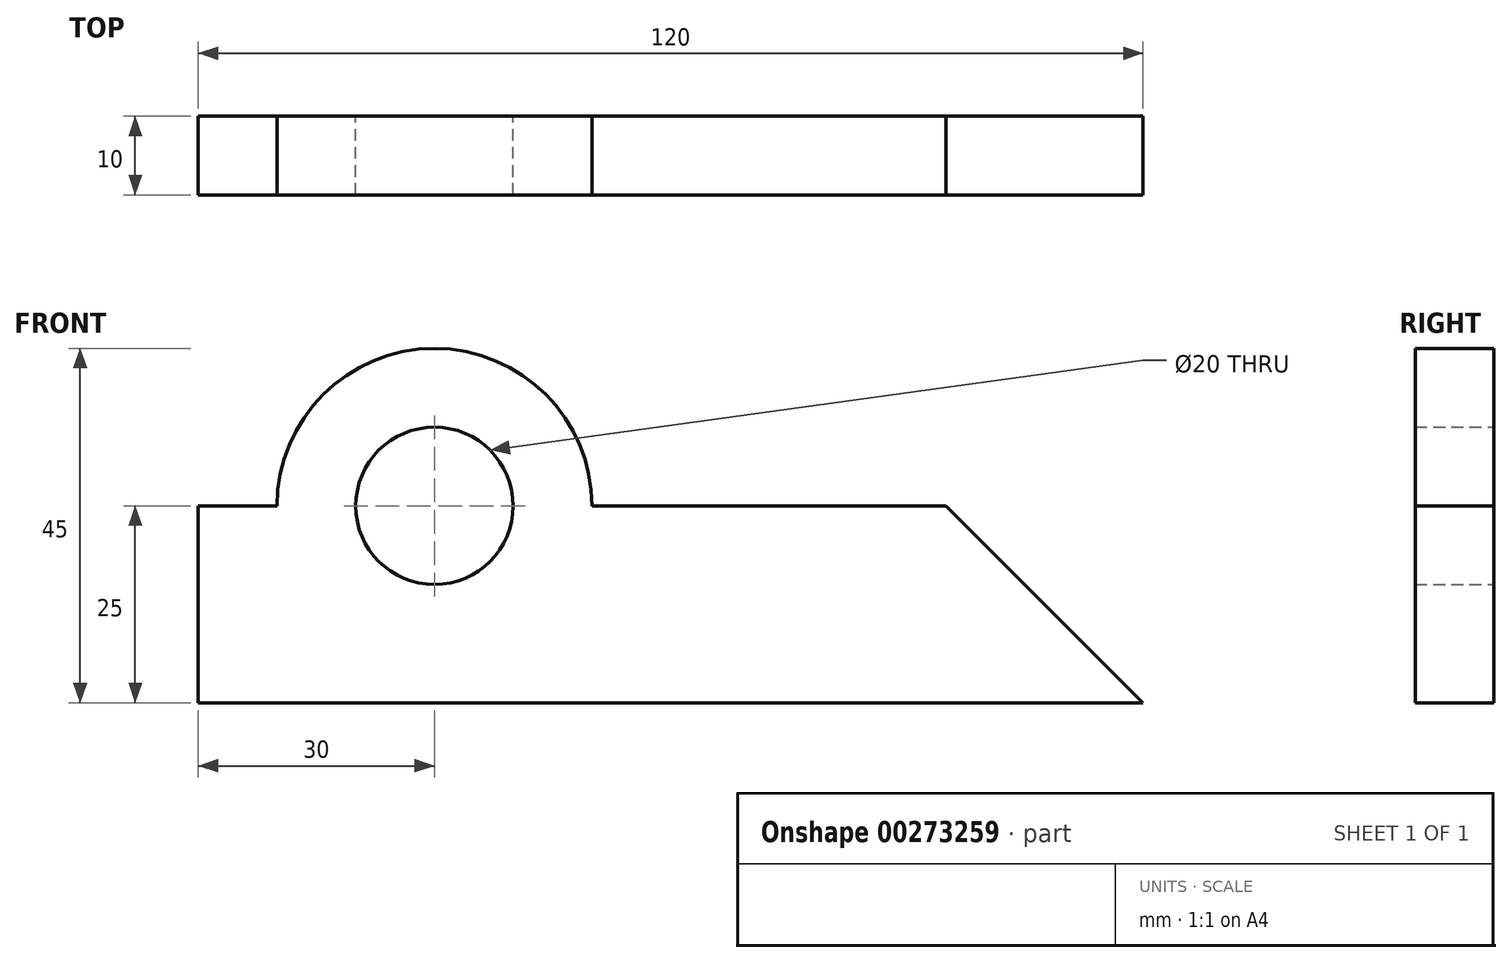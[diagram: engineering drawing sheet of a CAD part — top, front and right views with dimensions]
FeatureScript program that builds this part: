
annotation { "Feature Type Name" : "Feature", "Feature Type Description" : "" }
export const myFeature = defineFeature(function(context is Context, id is Id, definition is map)
    precondition{}
    {
        {
            var Q0;
            Q0=qCreatedBy(makeId("Front.planeOp"),FACE);
            var sketch = newSketch(context, id + "F0", { "sketchPlane" : qUnion([Q0])});
            skLineSegment(sketch, "E0", {"start": v(0, 0) * mm, "end": v(120, 0) * mm});
            skLineSegment(sketch, "E1", {"start": v(0, 0) * mm, "end": v(0, 25) * mm});
            skLineSegment(sketch, "E2", {"start": v(0, 25) * mm, "end": v(10, 25) * mm});
            skCircle(sketch, "E3", {"center": v(30, 25) * mm, "radius": 10 * mm});
            skArc(sketch, "E4", {"start": v(50, 25) * mm, "mid": v(30, 45) * mm, "end": v(10, 25) * mm});
            skLineSegment(sketch, "E5", {"start": v(120, 0) * mm, "end": v(95, 25) * mm});
            skLineSegment(sketch, "E6", {"start": v(50, 25) * mm, "end": v(95, 25) * mm});
            skSolve(sketch);
        }
        {
            var Q0;
            Q0=makeQuery(id+"F0.imprint","IMPRINT",FACE,{"disambiguationData":[TD([[makeQuery(id+"F0.imprint","IMPRINT",EDGE,{"derivedFrom":sQuery(id+"F0.wireOp",EDGE,"E0")}),1.0]])]});
            extrude(context, id + "F1", {"entities" : qUnion([Q0]), "depth" : 10 * mm});
        }
    });
